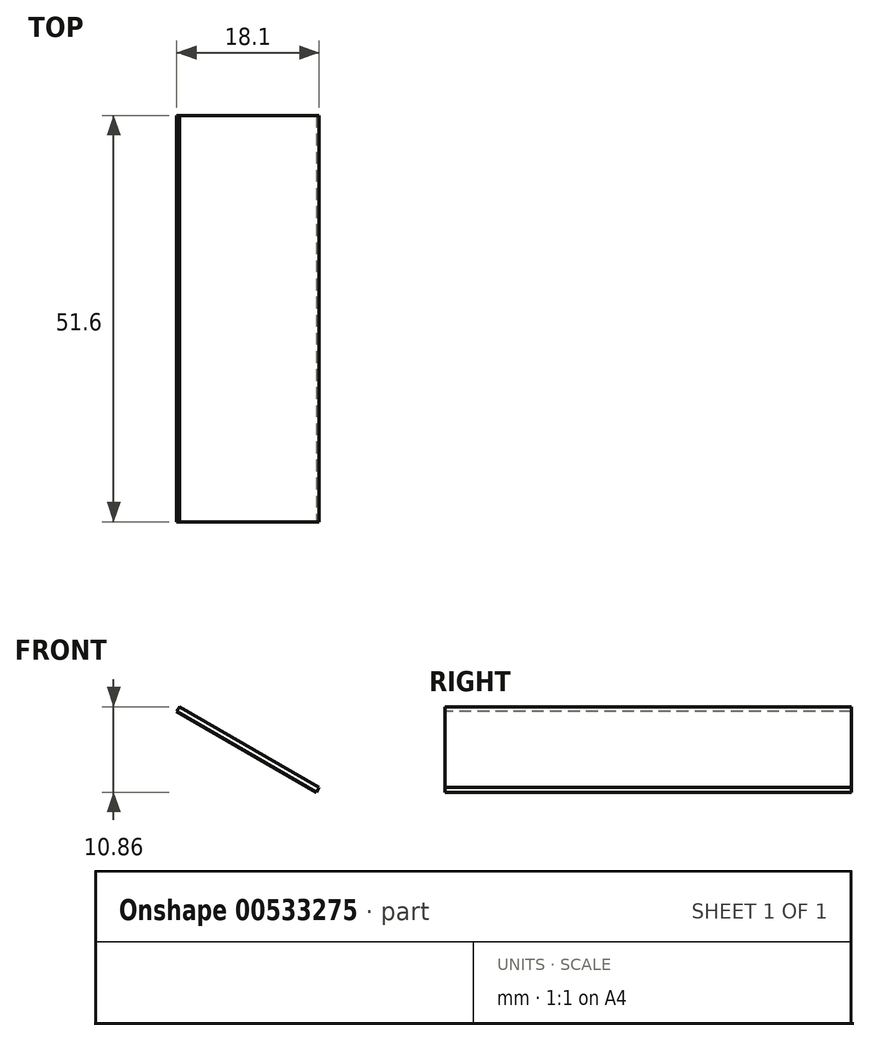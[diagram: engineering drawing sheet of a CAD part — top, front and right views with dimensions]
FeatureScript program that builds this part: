
annotation { "Feature Type Name" : "Feature", "Feature Type Description" : "" }
export const myFeature = defineFeature(function(context is Context, id is Id, definition is map)
    precondition{}
    {
        {
            var Q0;
            Q0=qCreatedBy(makeId("Top.planeOp"),FACE);
            var sketch = newSketch(context, id + "F0", { "sketchPlane" : qUnion([Q0])});
            skLineSegment(sketch, "E0.bottom", {"start": v(-0.5, 10) * mm, "end": v(20, 10) * mm});
            skLineSegment(sketch, "E0.top", {"start": v(-0.5, -41.6) * mm, "end": v(20, -41.6) * mm});
            skLineSegment(sketch, "E0.left", {"start": v(-0.5, 10) * mm, "end": v(-0.5, -41.6) * mm});
            skLineSegment(sketch, "E0.right", {"start": v(20, 10) * mm, "end": v(20, -41.6) * mm});
            skSolve(sketch);
        }
        {
            var Q0;
            Q0 = qSketchRegion(id + "F0", true);
            extrude(context, id + "F1", {"entities" : qUnion([Q0]), "depth" : 0.7 * mm, "offsetDistance" : 25 * mm});
        }
        {
            var Q0;
            Q0=makeQuery(id+"F1.opExtrude","SWEPT_BODY",BODY,{"disambiguationData":[OSD([sQuery(id+"F0.wireOp",EDGE,"E0.bottom"),sQuery(id+"F0.wireOp",EDGE,"E0.top"),sQuery(id+"F0.wireOp",EDGE,"E0.left"),sQuery(id+"F0.wireOp",EDGE,"E0.right")])]});
            var Q1;
            Q1=makeQuery(id+"F1.opExtrude","CAP_EDGE",EDGE,{"disambiguationData":[OSD([sQuery(id+"F0.wireOp",EDGE,"E0.right")])],"isStart":false});
            transform(context, id + "F2", {"entities" : qUnion([Q0]), "transformType" : TransformType.ROTATION, "transformAxis" : qUnion([Q1]), "angle" : 30 * degree, "oppositeDirection" : true, "makeCopy" : false});
        }
    });
